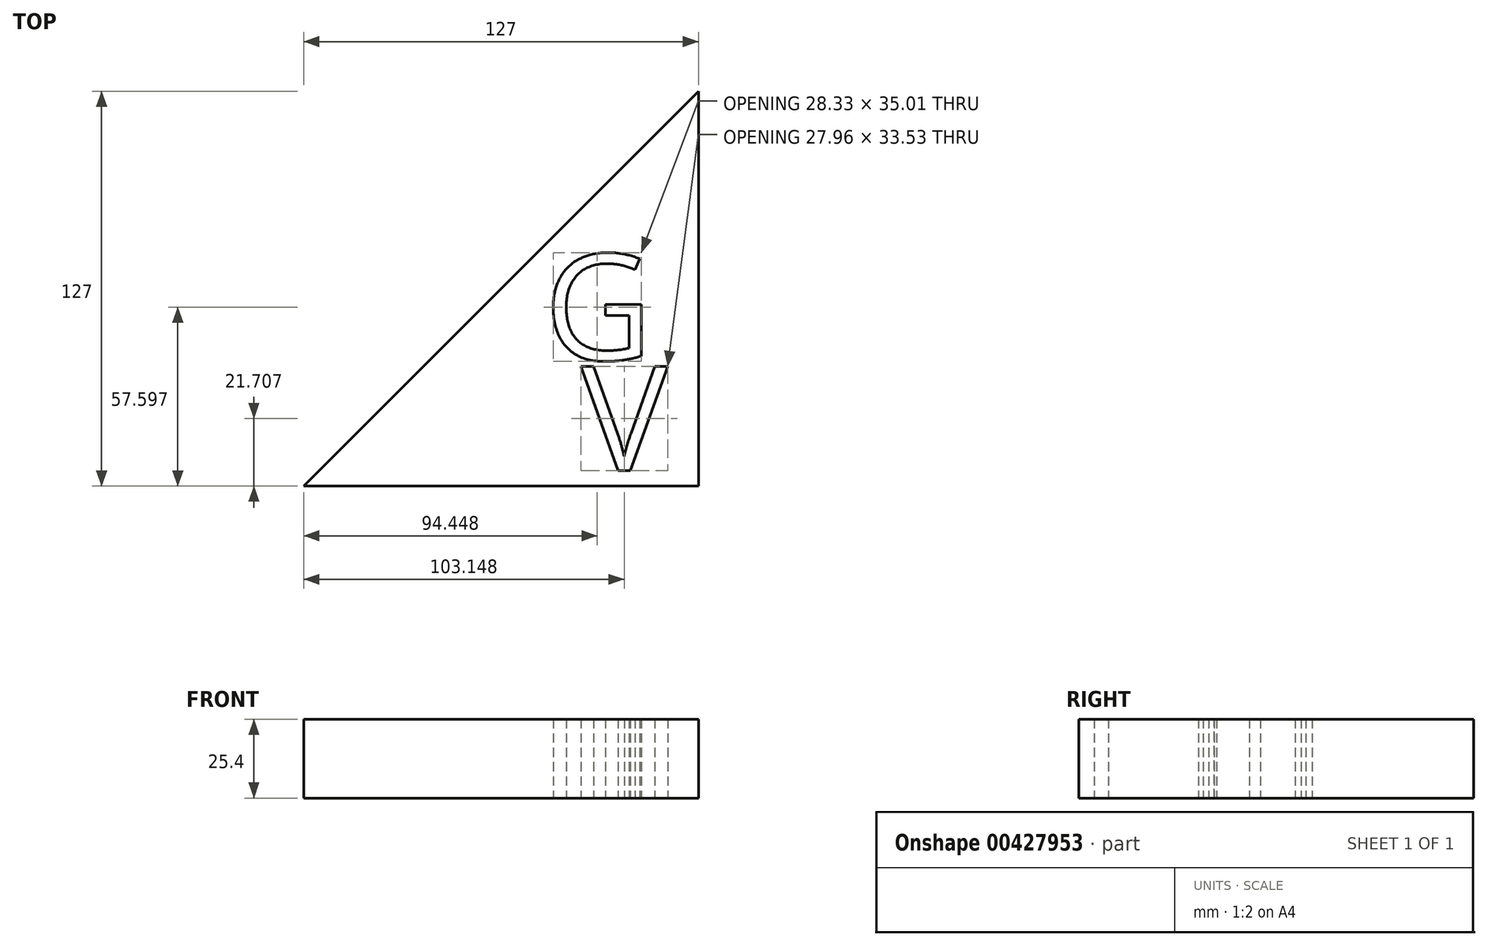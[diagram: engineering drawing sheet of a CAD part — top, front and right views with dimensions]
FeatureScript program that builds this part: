
annotation { "Feature Type Name" : "Feature", "Feature Type Description" : "" }
export const myFeature = defineFeature(function(context is Context, id is Id, definition is map)
    precondition{}
    {
        {
            var Q0;
            Q0=qCreatedBy(makeId("Top.planeOp"),FACE);
            var sketch = newSketch(context, id + "F0", { "sketchPlane" : qUnion([Q0])});
            skLineSegment(sketch, "E0", {"start": v(4.47, -54.37) * mm, "end": v(4.47, 72.63) * mm});
            skLineSegment(sketch, "E1", {"start": v(4.47, -54.37) * mm, "end": v(-122.53, -54.37) * mm});
            skLineSegment(sketch, "E2", {"start": v(-122.53, -54.37) * mm, "end": v(4.47, 72.63) * mm});
            skText(sketch, "E3", { "text": "G", "fontName": "OpenSans-Regular.ttf"});
            skText(sketch, "E4", { "text": "V", "fontName": "OpenSans-Regular.ttf"});
            const initialGuessF0  = {"E3": [-0.04516, -0.01381, 1, 0, 0.03435], "E4": [-0.03336, -0.04943, 1, 0, 0.03382]};
            skSetInitialGuess(sketch, initialGuessF0);
            skSolve(sketch);
        }
        {
            var Q0;
            Q0=qSketchRegion(id+"F0",true);
            extrude(context, id + "F1", {"entities" : qUnion([Q0]), "depth" : 25.4 * mm, "symmetric" : true});
        }
    });
